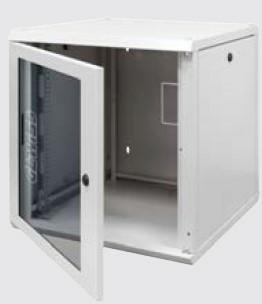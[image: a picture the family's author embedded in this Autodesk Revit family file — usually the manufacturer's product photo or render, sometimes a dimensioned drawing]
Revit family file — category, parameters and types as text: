
# Revit family: Domotics-NetworkCabling-GEWISS-CABINETS_WALL-MOUNTED_19_15U_D600
name_source: partatom
category: Apparecchi elettrici
units: mm (PartAtom-declared; Revit-internal decimal feet)

## family parameters
Condiviso = No
Host = Superficie
Mantenere orientamento annotazione = Sì
Punto di calcolo locali = Sì
Quota connettore circolare = Usa diametro
Taglio con vuoti quando caricato = No
Tipo di parte = Normale

## types (1)
- GW38419 - WALL CABINET 19 15U DEPTH 600MM.
    Cabling unity = 15 U
    Catalogue = DOMOTICS
    Category = 19â€ wall-mount cabinet
    Colour = Grey (RAL 7035)
    Depth (mm) = 600 mm
    Descrizione = WALL CABINET 19 15U DEPTH 600MM.
    Door opening = 180°
    Electrocod = 3752
    Finishing = Textured
    IDF = 0dbaedf6-5384-4bdc-ba3e-a0e6901a7229
    IDT = 875adcc69f394db3bb3f37c4bdb18b0a
    IP degree = IP20
    Immagine tipo = B.jpg
    Material = Steel
    Modello = GW38419
    No. uprights = 2
    Outer dim. LxHxD (mm) = 600x740x600
    Potenza quadro = 0 V
    Produttore = GEWISS S.p.A.
    Prospetto di default = 900 mm
    SEO = Board
    Static load capacity = 50KG
    Technical sheet = https://www.gewiss.com
    Type of door = Reversible
    URL = https://www.gewiss.com
    Version file RFA = 21.2
    n_poli = 1

## geometry (parser evidence)
native form markers: Sweep x4
no freeform markers — native parametric forms only
